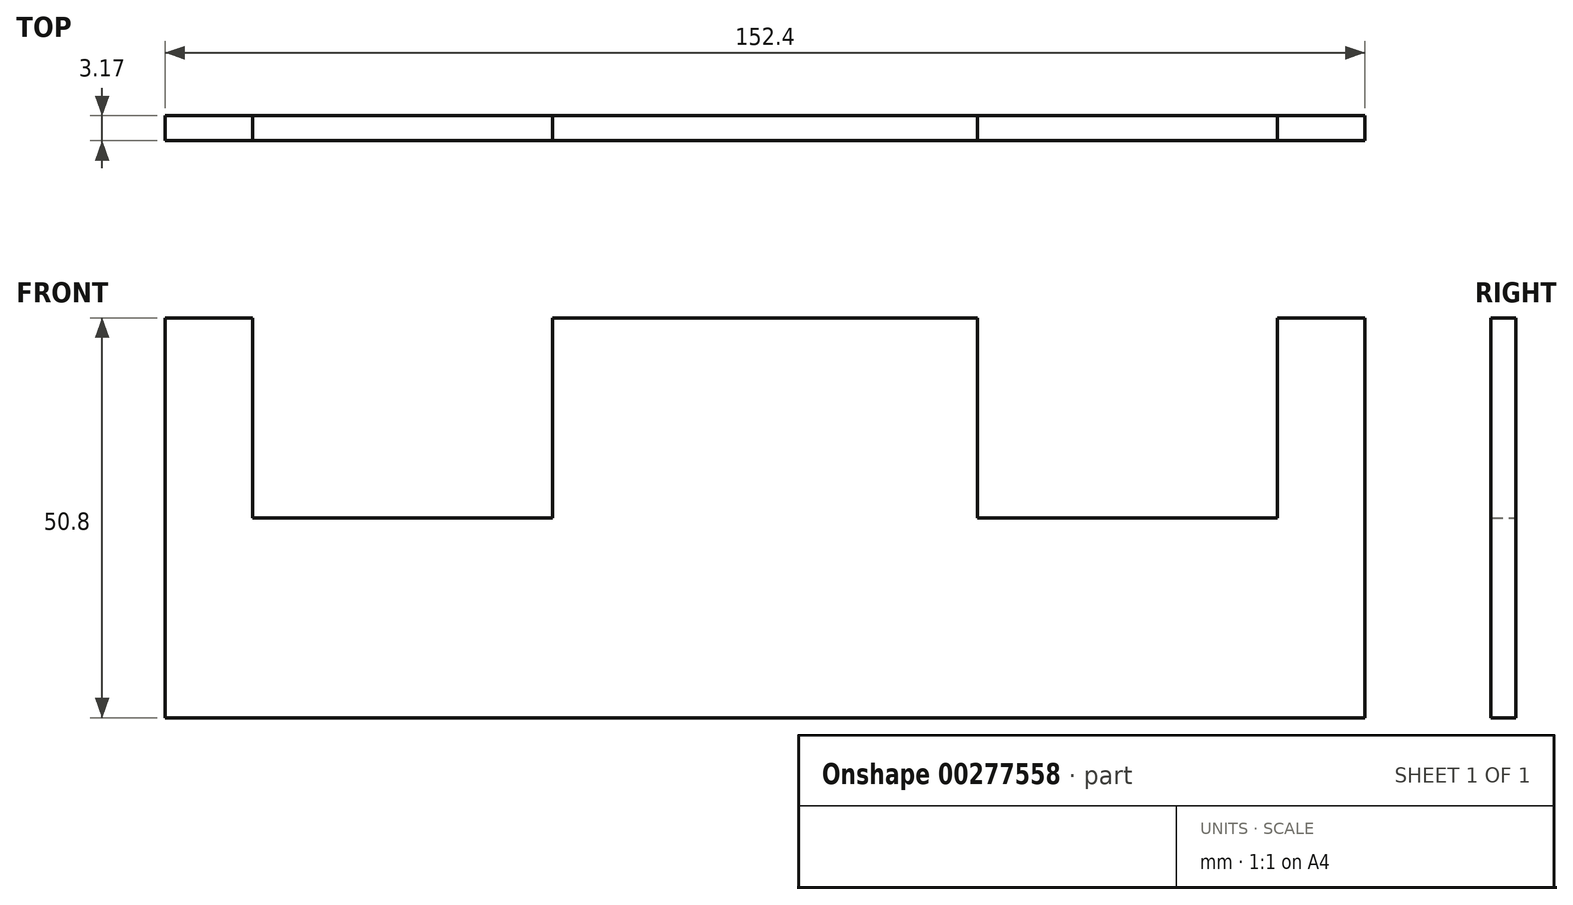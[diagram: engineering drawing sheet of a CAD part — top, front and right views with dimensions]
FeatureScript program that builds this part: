
annotation { "Feature Type Name" : "Feature", "Feature Type Description" : "" }
export const myFeature = defineFeature(function(context is Context, id is Id, definition is map)
    precondition{}
    {
        {
            var Q0;
            Q0=qCreatedBy(makeId("Front.planeOp"),FACE);
            var sketch = newSketch(context, id + "F0", { "sketchPlane" : qUnion([Q0])});
            skLineSegment(sketch, "E0.bottom", {"start": v(-60, 25.4) * mm, "end": v(-32.07, 25.4) * mm});
            skLineSegment(sketch, "E0.left", {"start": v(-65.09, 25.4) * mm, "end": v(-65.09, 0) * mm});
            skLineSegment(sketch, "E0.right", {"start": v(65.09, 25.4) * mm, "end": v(65.09, 0) * mm});
            skLineSegment(sketch, "E1.top", {"start": v(76.2, 25.4) * mm, "end": v(65.09, 25.4) * mm});
            skLineSegment(sketch, "E1.left", {"start": v(76.2, -25.4) * mm, "end": v(76.2, 25.4) * mm});
            skLineSegment(sketch, "E1.right", {"start": v(-76.2, -25.4) * mm, "end": v(-76.2, 25.4) * mm});
            skPoint(sketch, "E2", {"position": v(-65.09, 0) * mm});
            skPoint(sketch, "E3", {"position": v(65.09, 0) * mm});
            skLineSegment(sketch, "E4", {"start": v(-65.09, 0) * mm, "end": v(-26.99, 0) * mm});
            skLineSegment(sketch, "E5", {"start": v(65.09, 0) * mm, "end": v(26.99, 0) * mm});
            skLineSegment(sketch, "E6", {"start": v(26.99, 0) * mm, "end": v(26.99, 25.4) * mm});
            skLineSegment(sketch, "E7", {"start": v(-26.99, 0) * mm, "end": v(-26.99, 25.4) * mm});
            skLineSegment(sketch, "E8.bottom", {"start": v(32.07, 25.4) * mm, "end": v(60, 25.4) * mm});
            skLineSegment(sketch, "E8.top", {"start": v(26.99, 0) * mm, "end": v(65.09, 0) * mm});
            skLineSegment(sketch, "E8.left", {"start": v(26.99, 25.4) * mm, "end": v(26.99, 0) * mm});
            skLineSegment(sketch, "E9.bottom", {"start": v(-65.09, 25.4) * mm, "end": v(-26.99, 25.4) * mm});
            skLineSegment(sketch, "E9.right", {"start": v(-26.99, 25.4) * mm, "end": v(-26.99, 0) * mm});
            skPoint(sketch, "E0.top.start.orphan", {"position": v(-65.09, -25.4) * mm});
            skPoint(sketch, "E1.bottom.end.orphan", {"position": v(65.09, -25.4) * mm});
            skLineSegment(sketch, "E10", {"start": v(76.2, -25.4) * mm, "end": v(-76.2, -25.4) * mm});
            skLineSegment(sketch, "E11.top", {"start": v(-60, 0) * mm, "end": v(-32.07, 0) * mm});
            skLineSegment(sketch, "E11.left", {"start": v(-60, 25.4) * mm, "end": v(-60, 0) * mm});
            skLineSegment(sketch, "E11.right", {"start": v(-32.07, 25.4) * mm, "end": v(-32.07, 0) * mm});
            skLineSegment(sketch, "E12.top", {"start": v(32.07, 0) * mm, "end": v(60, 0) * mm});
            skLineSegment(sketch, "E12.left", {"start": v(32.07, 25.4) * mm, "end": v(32.07, 0) * mm});
            skLineSegment(sketch, "E12.right", {"start": v(60, 25.4) * mm, "end": v(60, 0) * mm});
            skLineSegment(sketch, "E13.trimOffspring", {"start": v(-65.09, 25.4) * mm, "end": v(-76.2, 25.4) * mm});
            skLineSegment(sketch, "E14.trimOffspring", {"start": v(-32.07, 25.4) * mm, "end": v(-60, 25.4) * mm});
            skLineSegment(sketch, "E15.trimOffspring", {"start": v(-26.99, 25.4) * mm, "end": v(26.99, 25.4) * mm});
            skLineSegment(sketch, "E16.trimOffspring", {"start": v(32.07, 25.4) * mm, "end": v(65.09, 25.4) * mm});
            skLineSegment(sketch, "E17.trimOffspring", {"start": v(60, 25.4) * mm, "end": v(-26.99, 25.4) * mm});
            skSolve(sketch);
        }
        {
            var Q0;
            Q0=makeQuery(id+"F0.imprint","IMPRINT",FACE,{"disambiguationData":[TD([[makeQuery(id+"F0.imprint","IMPRINT",EDGE,{"derivedFrom":sQuery(id+"F0.wireOp",EDGE,"E11.top")}),1.0]])]});
            var Q1;
            Q1=makeQuery(id+"F0.imprint","IMPRINT",FACE,{"disambiguationData":[TD([[makeQuery(id+"F0.imprint","IMPRINT",EDGE,{"derivedFrom":sQuery(id+"F0.wireOp",EDGE,"E12.top")}),1.0]])]});
            var Q2;
            Q2=makeQuery(id+"F0.imprint","IMPRINT",FACE,{"disambiguationData":[TD([[makeQuery(id+"F0.imprint","IMPRINT",EDGE,{"derivedFrom":sQuery(id+"F0.wireOp",EDGE,"E1.top")}),1.0]])]});
            extrude(context, id + "F1", {"entities" : qUnion([Q0, Q1, Q2]), "depth" : 3.17 * mm});
        }
    });
